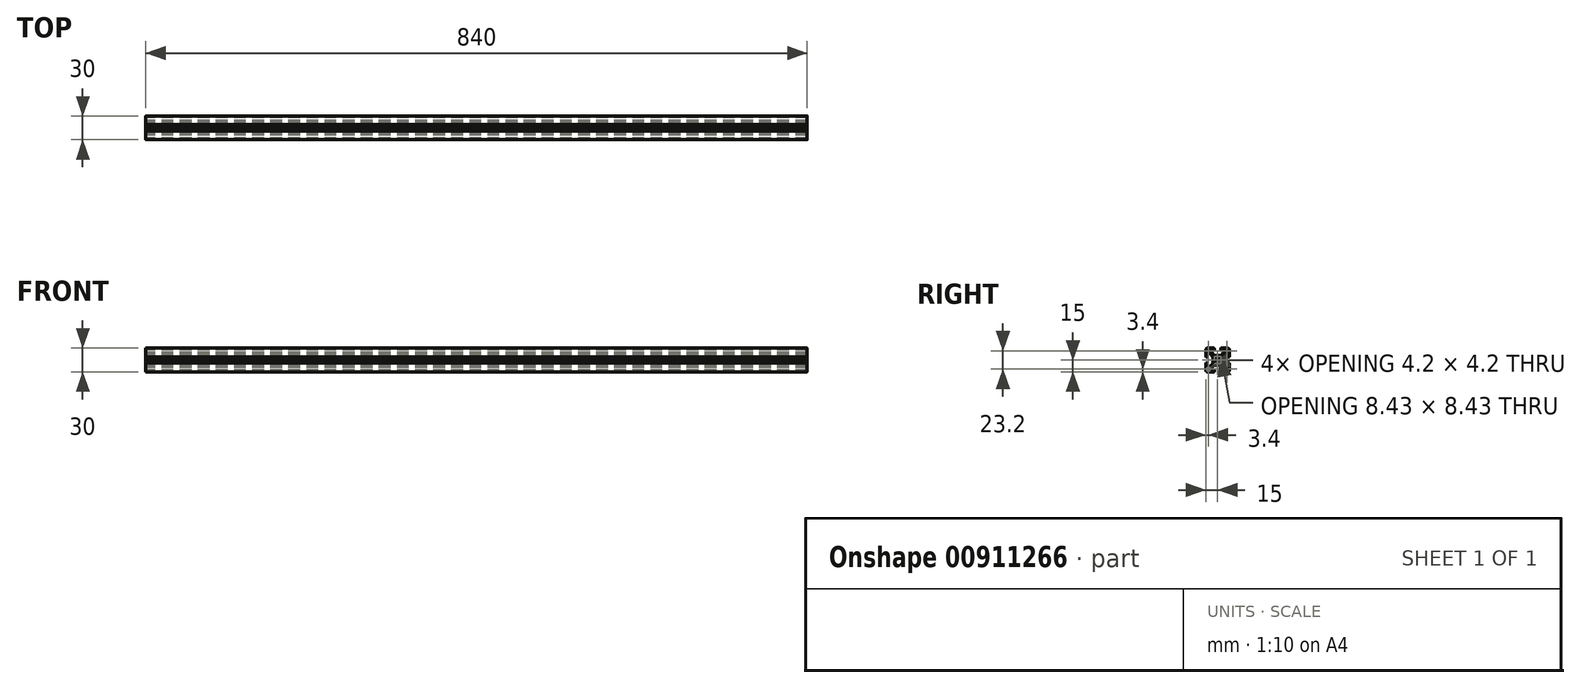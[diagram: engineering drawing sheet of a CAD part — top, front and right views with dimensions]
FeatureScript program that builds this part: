
annotation { "Feature Type Name" : "Feature", "Feature Type Description" : "" }
export const myFeature = defineFeature(function(context is Context, id is Id, definition is map)
    precondition{}
    {
        {
            var Q0;
            Q0=qCreatedBy(makeId("Right.planeOp"),FACE);
            var sketch = newSketch(context, id + "F0", { "sketchPlane" : qUnion([Q0])});
            skArc(sketch, "E0", {"start": v(9.88, 13.7) * mm, "mid": v(9.61, 13.59) * mm, "end": v(9.5, 13.32) * mm});
            skLineSegment(sketch, "E1", {"start": v(12.7, 13.7) * mm, "end": v(9.88, 13.7) * mm});
            skArc(sketch, "E2", {"start": v(13.7, 12.7) * mm, "mid": v(13.4, 13.4) * mm, "end": v(12.7, 13.7) * mm});
            skLineSegment(sketch, "E3", {"start": v(13.7, 9.88) * mm, "end": v(13.7, 12.7) * mm});
            skArc(sketch, "E4", {"start": v(13.32, 9.5) * mm, "mid": v(13.59, 9.61) * mm, "end": v(13.7, 9.88) * mm});
            skLineSegment(sketch, "E5", {"start": v(9.88, 9.5) * mm, "end": v(13.32, 9.5) * mm});
            skArc(sketch, "E6", {"start": v(9.5, 9.88) * mm, "mid": v(9.61, 9.61) * mm, "end": v(9.88, 9.5) * mm});
            skLineSegment(sketch, "E7", {"start": v(9.5, 13.32) * mm, "end": v(9.5, 9.88) * mm});
            skArc(sketch, "E8", {"start": v(-9.5, 13.32) * mm, "mid": v(-9.61, 13.59) * mm, "end": v(-9.88, 13.7) * mm});
            skLineSegment(sketch, "E9", {"start": v(-9.5, 9.88) * mm, "end": v(-9.5, 13.32) * mm});
            skArc(sketch, "E10", {"start": v(-9.88, 9.5) * mm, "mid": v(-9.61, 9.61) * mm, "end": v(-9.5, 9.88) * mm});
            skLineSegment(sketch, "E11", {"start": v(-13.32, 9.5) * mm, "end": v(-9.88, 9.5) * mm});
            skArc(sketch, "E12", {"start": v(-13.7, 9.88) * mm, "mid": v(-13.59, 9.61) * mm, "end": v(-13.32, 9.5) * mm});
            skLineSegment(sketch, "E13", {"start": v(-13.7, 12.7) * mm, "end": v(-13.7, 9.88) * mm});
            skArc(sketch, "E14", {"start": v(-12.7, 13.7) * mm, "mid": v(-13.4, 13.4) * mm, "end": v(-13.7, 12.7) * mm});
            skLineSegment(sketch, "E15", {"start": v(-9.88, 13.7) * mm, "end": v(-12.7, 13.7) * mm});
            skArc(sketch, "E16", {"start": v(-1.5, -3.2) * mm, "mid": v(0, -3.53) * mm, "end": v(1.5, -3.2) * mm});
            skLineSegment(sketch, "E17", {"start": v(-2.47, -3.98) * mm, "end": v(-1.5, -3.2) * mm});
            skArc(sketch, "E18", {"start": v(-3.98, -2.47) * mm, "mid": v(-3.9, -3.9) * mm, "end": v(-2.47, -3.98) * mm});
            skLineSegment(sketch, "E19", {"start": v(-3.2, -1.5) * mm, "end": v(-3.98, -2.47) * mm});
            skArc(sketch, "E20", {"start": v(-3.2, 1.5) * mm, "mid": v(-3.53, 0) * mm, "end": v(-3.2, -1.5) * mm});
            skLineSegment(sketch, "E21", {"start": v(-3.98, 2.47) * mm, "end": v(-3.2, 1.5) * mm});
            skArc(sketch, "E22", {"start": v(-2.47, 3.98) * mm, "mid": v(-3.9, 3.9) * mm, "end": v(-3.98, 2.47) * mm});
            skLineSegment(sketch, "E23", {"start": v(-1.5, 3.2) * mm, "end": v(-2.47, 3.98) * mm});
            skArc(sketch, "E24", {"start": v(1.5, 3.2) * mm, "mid": v(0, 3.53) * mm, "end": v(-1.5, 3.2) * mm});
            skLineSegment(sketch, "E25", {"start": v(2.47, 3.98) * mm, "end": v(1.5, 3.2) * mm});
            skArc(sketch, "E26", {"start": v(3.98, 2.47) * mm, "mid": v(3.9, 3.9) * mm, "end": v(2.47, 3.98) * mm});
            skLineSegment(sketch, "E27", {"start": v(3.2, 1.5) * mm, "end": v(3.98, 2.47) * mm});
            skArc(sketch, "E28", {"start": v(3.2, -1.5) * mm, "mid": v(3.53, 0) * mm, "end": v(3.2, 1.5) * mm});
            skLineSegment(sketch, "E29", {"start": v(3.98, -2.47) * mm, "end": v(3.2, -1.5) * mm});
            skArc(sketch, "E30", {"start": v(2.47, -3.98) * mm, "mid": v(3.9, -3.9) * mm, "end": v(3.98, -2.47) * mm});
            skLineSegment(sketch, "E31", {"start": v(1.5, -3.2) * mm, "end": v(2.47, -3.98) * mm});
            skArc(sketch, "E32", {"start": v(-13.32, -9.5) * mm, "mid": v(-13.59, -9.61) * mm, "end": v(-13.7, -9.88) * mm});
            skLineSegment(sketch, "E33", {"start": v(-9.88, -9.5) * mm, "end": v(-13.32, -9.5) * mm});
            skArc(sketch, "E34", {"start": v(-9.5, -9.88) * mm, "mid": v(-9.61, -9.61) * mm, "end": v(-9.88, -9.5) * mm});
            skLineSegment(sketch, "E35", {"start": v(-9.5, -13.32) * mm, "end": v(-9.5, -9.88) * mm});
            skArc(sketch, "E36", {"start": v(-9.88, -13.7) * mm, "mid": v(-9.61, -13.59) * mm, "end": v(-9.5, -13.32) * mm});
            skLineSegment(sketch, "E37", {"start": v(-12.7, -13.7) * mm, "end": v(-9.88, -13.7) * mm});
            skArc(sketch, "E38", {"start": v(-13.7, -12.7) * mm, "mid": v(-13.4, -13.4) * mm, "end": v(-12.7, -13.7) * mm});
            skLineSegment(sketch, "E39", {"start": v(-13.7, -9.88) * mm, "end": v(-13.7, -12.7) * mm});
            skArc(sketch, "E40", {"start": v(9.5, -13.32) * mm, "mid": v(9.61, -13.59) * mm, "end": v(9.88, -13.7) * mm});
            skLineSegment(sketch, "E41", {"start": v(9.5, -9.88) * mm, "end": v(9.5, -13.32) * mm});
            skArc(sketch, "E42", {"start": v(9.88, -9.5) * mm, "mid": v(9.61, -9.61) * mm, "end": v(9.5, -9.88) * mm});
            skLineSegment(sketch, "E43", {"start": v(13.32, -9.5) * mm, "end": v(9.88, -9.5) * mm});
            skArc(sketch, "E44", {"start": v(13.7, -9.88) * mm, "mid": v(13.59, -9.61) * mm, "end": v(13.32, -9.5) * mm});
            skLineSegment(sketch, "E45", {"start": v(13.7, -12.7) * mm, "end": v(13.7, -9.88) * mm});
            skArc(sketch, "E46", {"start": v(12.7, -13.7) * mm, "mid": v(13.4, -13.4) * mm, "end": v(13.7, -12.7) * mm});
            skLineSegment(sketch, "E47", {"start": v(9.88, -13.7) * mm, "end": v(12.7, -13.7) * mm});
            skArc(sketch, "E48", {"start": v(13.24, -4) * mm, "mid": v(12.89, -4.15) * mm, "end": v(12.74, -4.5) * mm});
            skLineSegment(sketch, "E49", {"start": v(12.74, -4.5) * mm, "end": v(12.74, -7.73) * mm});
            skArc(sketch, "E50", {"start": v(12.24, -8.25) * mm, "mid": v(12.6, -8.1) * mm, "end": v(12.74, -7.73) * mm});
            skLineSegment(sketch, "E51", {"start": v(12.24, -8.25) * mm, "end": v(10.26, -8.25) * mm});
            skArc(sketch, "E52", {"start": v(9.9, -8.1) * mm, "mid": v(10.07, -8.21) * mm, "end": v(10.26, -8.25) * mm});
            skLineSegment(sketch, "E53", {"start": v(9.9, -8.1) * mm, "end": v(5.98, -4.18) * mm});
            skArc(sketch, "E54", {"start": v(5.83, -3.82) * mm, "mid": v(5.87, -4.02) * mm, "end": v(5.98, -4.18) * mm});
            skLineSegment(sketch, "E55", {"start": v(5.83, -3.82) * mm, "end": v(5.83, -1.01) * mm});
            skLineSegment(sketch, "E56", {"start": v(5.83, -1.01) * mm, "end": v(5.32, -0.06) * mm});
            skLineSegment(sketch, "E57", {"start": v(5.32, -0.06) * mm, "end": v(5.83, 0.89) * mm});
            skLineSegment(sketch, "E58", {"start": v(5.83, 0.89) * mm, "end": v(5.83, 3.82) * mm});
            skArc(sketch, "E59", {"start": v(5.98, 4.18) * mm, "mid": v(5.87, 4.02) * mm, "end": v(5.83, 3.82) * mm});
            skLineSegment(sketch, "E60", {"start": v(5.98, 4.18) * mm, "end": v(9.9, 8.1) * mm});
            skArc(sketch, "E61", {"start": v(10.26, 8.25) * mm, "mid": v(10.07, 8.21) * mm, "end": v(9.9, 8.1) * mm});
            skLineSegment(sketch, "E62", {"start": v(10.26, 8.25) * mm, "end": v(12.24, 8.25) * mm});
            skArc(sketch, "E63", {"start": v(12.74, 7.73) * mm, "mid": v(12.6, 8.1) * mm, "end": v(12.24, 8.25) * mm});
            skLineSegment(sketch, "E64", {"start": v(12.74, 7.73) * mm, "end": v(12.74, 4.5) * mm});
            skArc(sketch, "E65", {"start": v(12.74, 4.5) * mm, "mid": v(12.89, 4.15) * mm, "end": v(13.24, 4) * mm});
            skLineSegment(sketch, "E66", {"start": v(13.24, 4) * mm, "end": v(14.5, 4) * mm});
            skArc(sketch, "E67", {"start": v(14.5, 4) * mm, "mid": v(14.85, 4.15) * mm, "end": v(15, 4.5) * mm});
            skLineSegment(sketch, "E68", {"start": v(15, 4.5) * mm, "end": v(15, 13) * mm});
            skArc(sketch, "E69", {"start": v(15, 13) * mm, "mid": v(14.41, 14.41) * mm, "end": v(13, 15) * mm});
            skLineSegment(sketch, "E70", {"start": v(13, 15) * mm, "end": v(4.5, 15) * mm});
            skArc(sketch, "E71", {"start": v(4.5, 15) * mm, "mid": v(4.15, 14.85) * mm, "end": v(4, 14.5) * mm});
            skLineSegment(sketch, "E72", {"start": v(4, 14.5) * mm, "end": v(4, 13.24) * mm});
            skArc(sketch, "E73", {"start": v(4, 13.24) * mm, "mid": v(4.15, 12.89) * mm, "end": v(4.5, 12.74) * mm});
            skLineSegment(sketch, "E74", {"start": v(4.5, 12.74) * mm, "end": v(7.73, 12.74) * mm});
            skArc(sketch, "E75", {"start": v(8.25, 12.24) * mm, "mid": v(8.1, 12.6) * mm, "end": v(7.73, 12.74) * mm});
            skLineSegment(sketch, "E76", {"start": v(8.25, 12.24) * mm, "end": v(8.25, 10.26) * mm});
            skArc(sketch, "E77", {"start": v(8.1, 9.9) * mm, "mid": v(8.21, 10.07) * mm, "end": v(8.25, 10.26) * mm});
            skLineSegment(sketch, "E78", {"start": v(8.1, 9.9) * mm, "end": v(4.18, 5.98) * mm});
            skArc(sketch, "E79", {"start": v(3.82, 5.83) * mm, "mid": v(4.02, 5.87) * mm, "end": v(4.18, 5.98) * mm});
            skLineSegment(sketch, "E80", {"start": v(3.82, 5.83) * mm, "end": v(0.95, 5.83) * mm});
            skLineSegment(sketch, "E81", {"start": v(0.95, 5.83) * mm, "end": v(0, 5.32) * mm});
            skLineSegment(sketch, "E82", {"start": v(0, 5.32) * mm, "end": v(-0.95, 5.83) * mm});
            skLineSegment(sketch, "E83", {"start": v(-0.95, 5.83) * mm, "end": v(-3.82, 5.83) * mm});
            skArc(sketch, "E84", {"start": v(-4.18, 5.98) * mm, "mid": v(-4.02, 5.87) * mm, "end": v(-3.82, 5.83) * mm});
            skLineSegment(sketch, "E85", {"start": v(-4.18, 5.98) * mm, "end": v(-8.1, 9.9) * mm});
            skArc(sketch, "E86", {"start": v(-8.25, 10.26) * mm, "mid": v(-8.21, 10.07) * mm, "end": v(-8.1, 9.9) * mm});
            skLineSegment(sketch, "E87", {"start": v(-8.25, 10.26) * mm, "end": v(-8.25, 12.24) * mm});
            skArc(sketch, "E88", {"start": v(-7.73, 12.74) * mm, "mid": v(-8.1, 12.6) * mm, "end": v(-8.25, 12.24) * mm});
            skLineSegment(sketch, "E89", {"start": v(-7.73, 12.74) * mm, "end": v(-4.5, 12.74) * mm});
            skArc(sketch, "E90", {"start": v(-4.5, 12.74) * mm, "mid": v(-4.15, 12.89) * mm, "end": v(-4, 13.24) * mm});
            skLineSegment(sketch, "E91", {"start": v(-4, 13.24) * mm, "end": v(-4, 14.5) * mm});
            skArc(sketch, "E92", {"start": v(-4, 14.5) * mm, "mid": v(-4.15, 14.85) * mm, "end": v(-4.5, 15) * mm});
            skLineSegment(sketch, "E93", {"start": v(-4.5, 15) * mm, "end": v(-13, 15) * mm});
            skArc(sketch, "E94", {"start": v(-13, 15) * mm, "mid": v(-14.41, 14.41) * mm, "end": v(-15, 13) * mm});
            skLineSegment(sketch, "E95", {"start": v(-15, 13) * mm, "end": v(-15, 4.5) * mm});
            skArc(sketch, "E96", {"start": v(-15, 4.5) * mm, "mid": v(-14.85, 4.15) * mm, "end": v(-14.5, 4) * mm});
            skLineSegment(sketch, "E97", {"start": v(-14.5, 4) * mm, "end": v(-13.24, 4) * mm});
            skArc(sketch, "E98", {"start": v(-13.24, 4) * mm, "mid": v(-12.89, 4.15) * mm, "end": v(-12.74, 4.5) * mm});
            skLineSegment(sketch, "E99", {"start": v(-12.74, 4.5) * mm, "end": v(-12.74, 7.73) * mm});
            skArc(sketch, "E100", {"start": v(-12.24, 8.25) * mm, "mid": v(-12.6, 8.1) * mm, "end": v(-12.74, 7.73) * mm});
            skLineSegment(sketch, "E101", {"start": v(-12.24, 8.25) * mm, "end": v(-10.26, 8.25) * mm});
            skArc(sketch, "E102", {"start": v(-9.9, 8.1) * mm, "mid": v(-10.07, 8.21) * mm, "end": v(-10.26, 8.25) * mm});
            skLineSegment(sketch, "E103", {"start": v(-9.9, 8.1) * mm, "end": v(-5.98, 4.18) * mm});
            skArc(sketch, "E104", {"start": v(-5.83, 3.82) * mm, "mid": v(-5.87, 4.02) * mm, "end": v(-5.98, 4.18) * mm});
            skLineSegment(sketch, "E105", {"start": v(-5.83, 3.82) * mm, "end": v(-5.83, 0.89) * mm});
            skLineSegment(sketch, "E106", {"start": v(-5.83, 0.89) * mm, "end": v(-5.32, -0.06) * mm});
            skLineSegment(sketch, "E107", {"start": v(-5.32, -0.06) * mm, "end": v(-5.83, -1.01) * mm});
            skLineSegment(sketch, "E108", {"start": v(-5.83, -1.01) * mm, "end": v(-5.83, -3.82) * mm});
            skArc(sketch, "E109", {"start": v(-5.98, -4.18) * mm, "mid": v(-5.87, -4.02) * mm, "end": v(-5.83, -3.82) * mm});
            skLineSegment(sketch, "E110", {"start": v(-5.98, -4.18) * mm, "end": v(-9.9, -8.1) * mm});
            skArc(sketch, "E111", {"start": v(-10.26, -8.25) * mm, "mid": v(-10.07, -8.21) * mm, "end": v(-9.9, -8.1) * mm});
            skLineSegment(sketch, "E112", {"start": v(-10.26, -8.25) * mm, "end": v(-12.24, -8.25) * mm});
            skArc(sketch, "E113", {"start": v(-12.74, -7.73) * mm, "mid": v(-12.6, -8.1) * mm, "end": v(-12.24, -8.25) * mm});
            skLineSegment(sketch, "E114", {"start": v(-12.74, -7.73) * mm, "end": v(-12.74, -4.5) * mm});
            skArc(sketch, "E115", {"start": v(-12.74, -4.5) * mm, "mid": v(-12.89, -4.15) * mm, "end": v(-13.24, -4) * mm});
            skLineSegment(sketch, "E116", {"start": v(-13.24, -4) * mm, "end": v(-14.5, -4) * mm});
            skArc(sketch, "E117", {"start": v(-14.5, -4) * mm, "mid": v(-14.85, -4.15) * mm, "end": v(-15, -4.5) * mm});
            skLineSegment(sketch, "E118", {"start": v(-15, -4.5) * mm, "end": v(-15, -13) * mm});
            skArc(sketch, "E119", {"start": v(-15, -13) * mm, "mid": v(-14.41, -14.41) * mm, "end": v(-13, -15) * mm});
            skLineSegment(sketch, "E120", {"start": v(-13, -15) * mm, "end": v(-4.5, -15) * mm});
            skArc(sketch, "E121", {"start": v(-4.5, -15) * mm, "mid": v(-4.15, -14.85) * mm, "end": v(-4, -14.5) * mm});
            skLineSegment(sketch, "E122", {"start": v(-4, -14.5) * mm, "end": v(-4, -13.24) * mm});
            skArc(sketch, "E123", {"start": v(-4, -13.24) * mm, "mid": v(-4.15, -12.89) * mm, "end": v(-4.5, -12.74) * mm});
            skLineSegment(sketch, "E124", {"start": v(-4.5, -12.74) * mm, "end": v(-7.73, -12.74) * mm});
            skArc(sketch, "E125", {"start": v(-8.25, -12.24) * mm, "mid": v(-8.1, -12.6) * mm, "end": v(-7.73, -12.74) * mm});
            skLineSegment(sketch, "E126", {"start": v(-8.25, -12.24) * mm, "end": v(-8.25, -10.26) * mm});
            skArc(sketch, "E127", {"start": v(-8.1, -9.9) * mm, "mid": v(-8.21, -10.07) * mm, "end": v(-8.25, -10.26) * mm});
            skLineSegment(sketch, "E128", {"start": v(-8.1, -9.9) * mm, "end": v(-4.18, -5.98) * mm});
            skArc(sketch, "E129", {"start": v(-3.82, -5.83) * mm, "mid": v(-4.02, -5.87) * mm, "end": v(-4.18, -5.98) * mm});
            skLineSegment(sketch, "E130", {"start": v(-3.82, -5.83) * mm, "end": v(-0.95, -5.83) * mm});
            skLineSegment(sketch, "E131", {"start": v(-0.95, -5.83) * mm, "end": v(0, -5.32) * mm});
            skLineSegment(sketch, "E132", {"start": v(0, -5.32) * mm, "end": v(0.95, -5.83) * mm});
            skLineSegment(sketch, "E133", {"start": v(0.95, -5.83) * mm, "end": v(3.82, -5.83) * mm});
            skArc(sketch, "E134", {"start": v(4.18, -5.98) * mm, "mid": v(4.02, -5.87) * mm, "end": v(3.82, -5.83) * mm});
            skLineSegment(sketch, "E135", {"start": v(4.18, -5.98) * mm, "end": v(8.1, -9.9) * mm});
            skArc(sketch, "E136", {"start": v(8.25, -10.26) * mm, "mid": v(8.21, -10.07) * mm, "end": v(8.1, -9.9) * mm});
            skLineSegment(sketch, "E137", {"start": v(8.25, -10.26) * mm, "end": v(8.25, -12.24) * mm});
            skArc(sketch, "E138", {"start": v(7.73, -12.74) * mm, "mid": v(8.1, -12.6) * mm, "end": v(8.25, -12.24) * mm});
            skLineSegment(sketch, "E139", {"start": v(7.73, -12.74) * mm, "end": v(4.5, -12.74) * mm});
            skArc(sketch, "E140", {"start": v(4.5, -12.74) * mm, "mid": v(4.15, -12.89) * mm, "end": v(4, -13.24) * mm});
            skLineSegment(sketch, "E141", {"start": v(4, -13.24) * mm, "end": v(4, -14.5) * mm});
            skArc(sketch, "E142", {"start": v(4, -14.5) * mm, "mid": v(4.15, -14.85) * mm, "end": v(4.5, -15) * mm});
            skLineSegment(sketch, "E143", {"start": v(4.5, -15) * mm, "end": v(13, -15) * mm});
            skArc(sketch, "E144", {"start": v(13, -15) * mm, "mid": v(14.41, -14.41) * mm, "end": v(15, -13) * mm});
            skLineSegment(sketch, "E145", {"start": v(15, -13) * mm, "end": v(15, -4.5) * mm});
            skArc(sketch, "E146", {"start": v(15, -4.5) * mm, "mid": v(14.85, -4.15) * mm, "end": v(14.5, -4) * mm});
            skLineSegment(sketch, "E147", {"start": v(14.5, -4) * mm, "end": v(13.24, -4) * mm});
            skSolve(sketch);
        }
        {
            var Q0;
            Q0 = qSketchRegion(id + "F0", true);
            extrude(context, id + "F1", {"entities" : qUnion([Q0]), "endBound" : BoundingType.SYMMETRIC, "depth" : (140 * 6) * mm, "offsetDistance" : 25 * mm});
        }
    });
